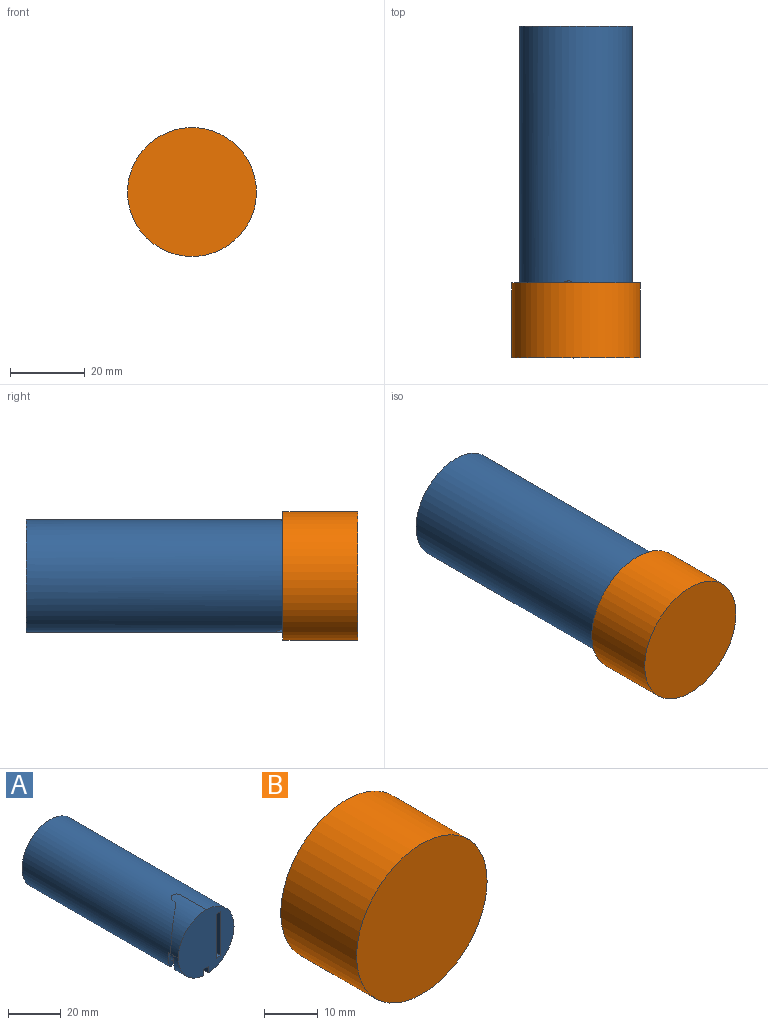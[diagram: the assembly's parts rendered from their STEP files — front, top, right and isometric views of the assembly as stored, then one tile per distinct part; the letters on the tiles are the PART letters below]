
ASSEMBLY  parts=2 mates=1
PART A: 26 faces, bbox 33.2x84x33 mm
  f0: plane 30x29.95mm, normal (0,-1,0), area 648.2mm2, adj f1,f2,f3,f5,f6,f7,f8,f14
  f1: cylinder r=15mm len=84mm, axis (0,1,0), area 7466.5mm2, adj f0,f2,f4,f15,f16,f17,f18,f19
  f2: cylinder r=15mm len=16mm, axis (0,1,0), area 196.4mm2, adj f0,f1,f3,f15
  f3: cylinder r=15mm len=14.95mm, axis (0,1,0), area 141.3mm2, adj f0,f2,f10,f11,f12,f13,f14
  f4: plane 30x30mm, normal (0,1,0), area 706.9mm2, adj f1
  f5: plane 25x2.5mm, normal (0,0,1), area 62.5mm2, adj f0,f6,f8,f9
  f6: plane 25x20.5mm, normal (-1,0,0), area 512.5mm2, adj f0,f5,f7,f9
  f7: plane 25x2.5mm, normal (0,0,-1), area 62.5mm2, adj f0,f6,f8,f9
  f8: plane 25x20.5mm, normal (1,0,0), area 512.5mm2, adj f0,f5,f7,f9
  f9: plane 20.5x2.5mm, normal (0,-1,0), area 51.2mm2, adj f5,f6,f7,f8
  f10: bspline ~6.11x2.34mm, area 5.7mm2, adj f3,f11,f14,f22
  f11: plane 2.84x0.98mm, normal (-0.96,0,0.27), area 2.9mm2, adj f3,f10,f12,f23
  f12: bspline ~6.19x3mm, area 9.1mm2, adj f3,f11,f13,f24
  f13: bspline ~15.01x11.74mm, area 64.9mm2, adj f3,f12,f15,f25
  f14: plane 14x2.95mm, normal (1,0,0), area 41.3mm2, adj f0,f3,f10,f21
  f15: plane 3.95x3.23mm, normal (0,0,-1), area 7.5mm2, adj f1,f2,f13,f20,f25
  f16: plane 14x2.95mm, normal (-1,0,0), area 41.3mm2, adj f0,f1,f17,f21
  f17: bspline ~7.25x6.77mm, area 29.4mm2, adj f1,f16,f18,f22
  f18: plane 2.84x0.98mm, normal (0.96,0,-0.27), area 2.9mm2, adj f1,f17,f19,f23
  f19: bspline ~2.9x1.09mm, area 1.8mm2, adj f1,f18,f20,f24
  f20: bspline ~16.91x13.58mm, area 45.9mm2, adj f1,f15,f19,f25
  f21: plane 14x2.5mm, normal (0,0,-1), area 35mm2, adj f0,f14,f16,f22
  f22: bspline ~5.66x3.05mm, area 13.4mm2, adj f10,f17,f21,f23
  f23: plane 2.41x0.98mm, normal (-0.27,0,-0.96), area 2.5mm2, adj f11,f18,f22,f24
  f24: bspline ~2.65x2.5mm, area 4.3mm2, adj f12,f19,f23,f25
  f25: bspline ~11.49x9.7mm, area 41.3mm2, adj f13,f15,f20,f24
PART B: 7 faces, bbox 34.4x20x34.4 mm
  f0: cylinder r=17.2mm len=34.4mm, axis (0,-1,0), area 2161.4mm2, adj f1,f2
  f1: plane 34.4x34.4mm, normal (0,1,0), area 203.6mm2, adj f0,f3
  f2: plane 34.4x34.4mm, normal (0,-1,0), area 929.4mm2, adj f0
  f3: cylinder r=15.2mm len=30.4mm, axis (0,-1,0), area 1715.9mm2, adj f1,f4,f5
  f4: plane 30.4x30.4mm, normal (0,1,0), area 725.8mm2, adj f3
  f5: cylinder r=1mm len=3.2mm, axis (0,0,1), area 20mm2, adj f3,f6
  f6: plane 2x2mm, normal (0,0,1), area 3.1mm2, adj f5
PLACE A at identity fixed
PLACE B rot(axis=(0,-1,0),148deg) t=(0,5.5,0)mm
MATE cylindrical B.f0 <-> A.f1  axis (0,-1,0) through (0,-77.5,0)mm
